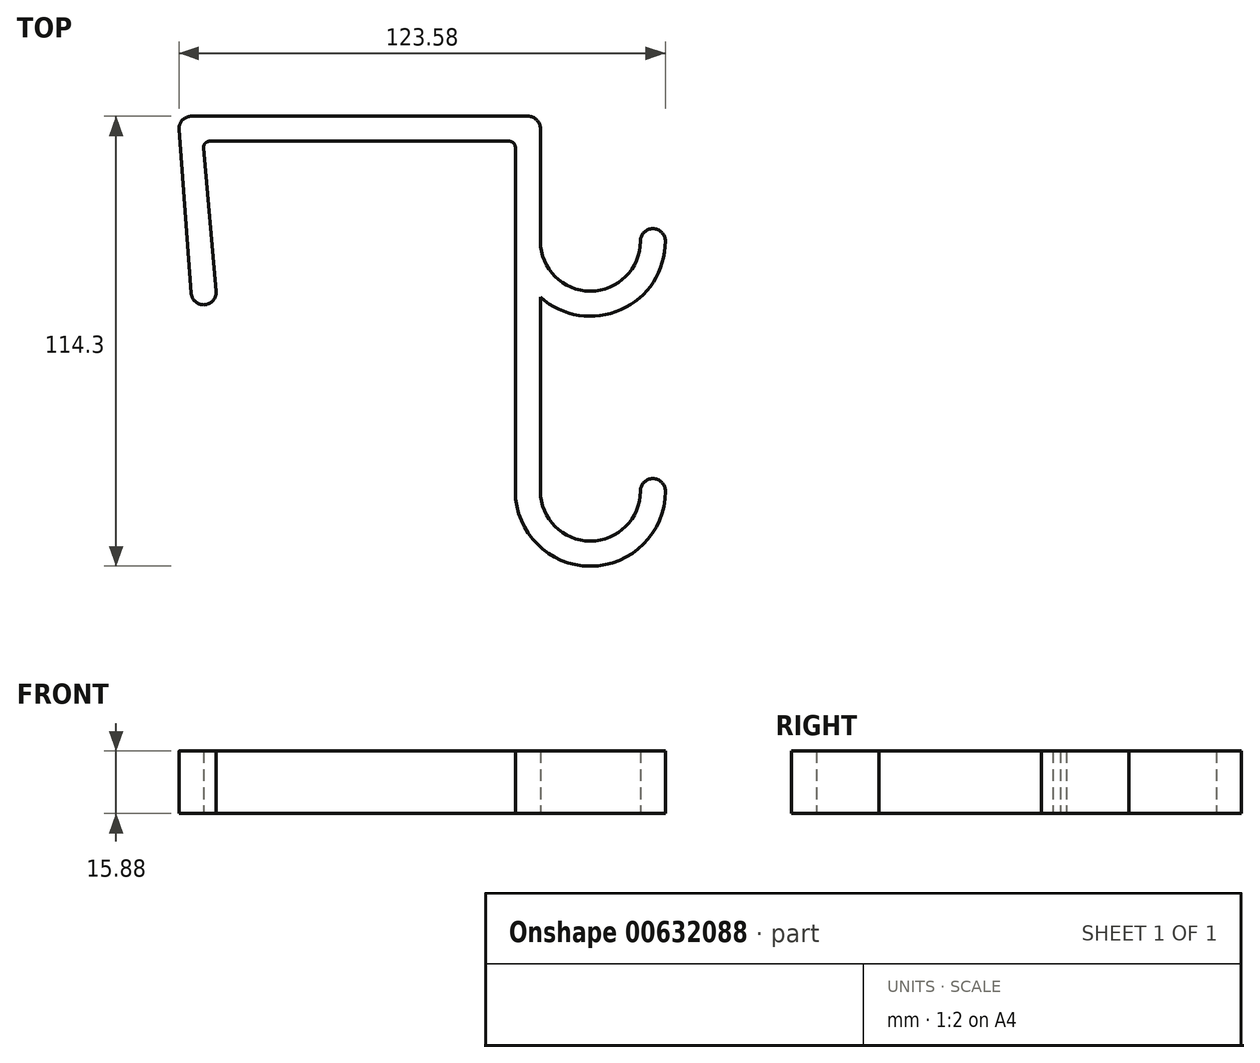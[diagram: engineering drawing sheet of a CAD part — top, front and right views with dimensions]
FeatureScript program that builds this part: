
annotation { "Feature Type Name" : "Feature", "Feature Type Description" : "" }
export const myFeature = defineFeature(function(context is Context, id is Id, definition is map)
    precondition{}
    {
        {
            var Q0;
            Q0=qCreatedBy(makeId("Top.planeOp"),FACE);
            var sketch = newSketch(context, id + "F0", { "sketchPlane" : qUnion([Q0])});
            skLineSegment(sketch, "E0", {"start": v(3.42, 0) * mm, "end": v(88.9, 0) * mm});
            skLineSegment(sketch, "E1", {"start": v(0.25, -3.41) * mm, "end": v(3.35, -44.96) * mm});
            skLineSegment(sketch, "E2", {"start": v(6.52, -47.9) * mm, "end": v(6.52, -47.9) * mm});
            skLineSegment(sketch, "E3", {"start": v(8.08, -6.35) * mm, "end": v(84.14, -6.35) * mm});
            skPoint(sketch, "E4.visualSharp", {"position": v(85.73, -6.35) * mm});
            skPoint(sketch, "E5.visualSharp", {"position": v(0, 0) * mm});
            skArc(sketch, "E5.filletArc", {"start": v(3.42, 0) * mm, "mid": v(1.1, -1.02) * mm, "end": v(0.25, -3.41) * mm});
            skPoint(sketch, "E6.visualSharp", {"position": v(3.57, -47.9) * mm});
            skArc(sketch, "E6.filletArc", {"start": v(3.35, -44.96) * mm, "mid": v(4.36, -47.05) * mm, "end": v(6.52, -47.9) * mm});
            skLineSegment(sketch, "E7", {"start": v(85.73, -7.94) * mm, "end": v(85.72, -95.25) * mm});
            skLineSegment(sketch, "E8", {"start": v(6.5, -8.08) * mm, "end": v(9.68, -44.45) * mm});
            skPoint(sketch, "E9.visualSharp", {"position": v(9.99, -47.9) * mm});
            skArc(sketch, "E9.filletArc", {"start": v(6.52, -47.9) * mm, "mid": v(8.86, -46.87) * mm, "end": v(9.68, -44.45) * mm});
            skArc(sketch, "E10", {"start": v(92.08, -31.75) * mm, "mid": v(104.78, -44.45) * mm, "end": v(117.48, -31.75) * mm});
            skArc(sketch, "E11", {"start": v(92.08, -95.25) * mm, "mid": v(104.78, -107.95) * mm, "end": v(117.48, -95.25) * mm});
            skArc(sketch, "E12", {"start": v(92.07, -45.95) * mm, "mid": v(112.55, -49.14) * mm, "end": v(123.83, -31.75) * mm});
            skArc(sketch, "E13", {"start": v(85.73, -95.25) * mm, "mid": v(104.78, -114.3) * mm, "end": v(123.83, -95.25) * mm});
            skLineSegment(sketch, "E14", {"start": v(92.08, -3.18) * mm, "end": v(92.08, -31.75) * mm});
            skArc(sketch, "E15", {"start": v(123.82, -31.75) * mm, "mid": v(120.65, -28.57) * mm, "end": v(117.47, -31.75) * mm});
            skArc(sketch, "E16", {"start": v(123.82, -95.25) * mm, "mid": v(120.65, -92.08) * mm, "end": v(117.47, -95.25) * mm});
            skLineSegment(sketch, "E17", {"start": v(92.07, -45.95) * mm, "end": v(92.07, -95.25) * mm});
            skPoint(sketch, "E18.visualSharp", {"position": v(6.35, -6.35) * mm});
            skArc(sketch, "E18.filletArc", {"start": v(8.08, -6.35) * mm, "mid": v(6.91, -6.87) * mm, "end": v(6.5, -8.08) * mm});
            skPoint(sketch, "E19.visualSharp", {"position": v(92.08, 0) * mm});
            skArc(sketch, "E19.filletArc", {"start": v(92.08, -3.18) * mm, "mid": v(91.15, -0.93) * mm, "end": v(88.9, 0) * mm});
            skArc(sketch, "E20.filletArc", {"start": v(85.73, -7.94) * mm, "mid": v(85.26, -6.81) * mm, "end": v(84.14, -6.35) * mm});
            skSolve(sketch);
        }
        {
            var Q0;
            Q0 = qSketchRegion(id + "F0", true);
            extrude(context, id + "F1", {"entities" : qUnion([Q0]), "depth" : 15.88 * mm, "offsetDistance" : 25.4 * mm});
        }
    });
